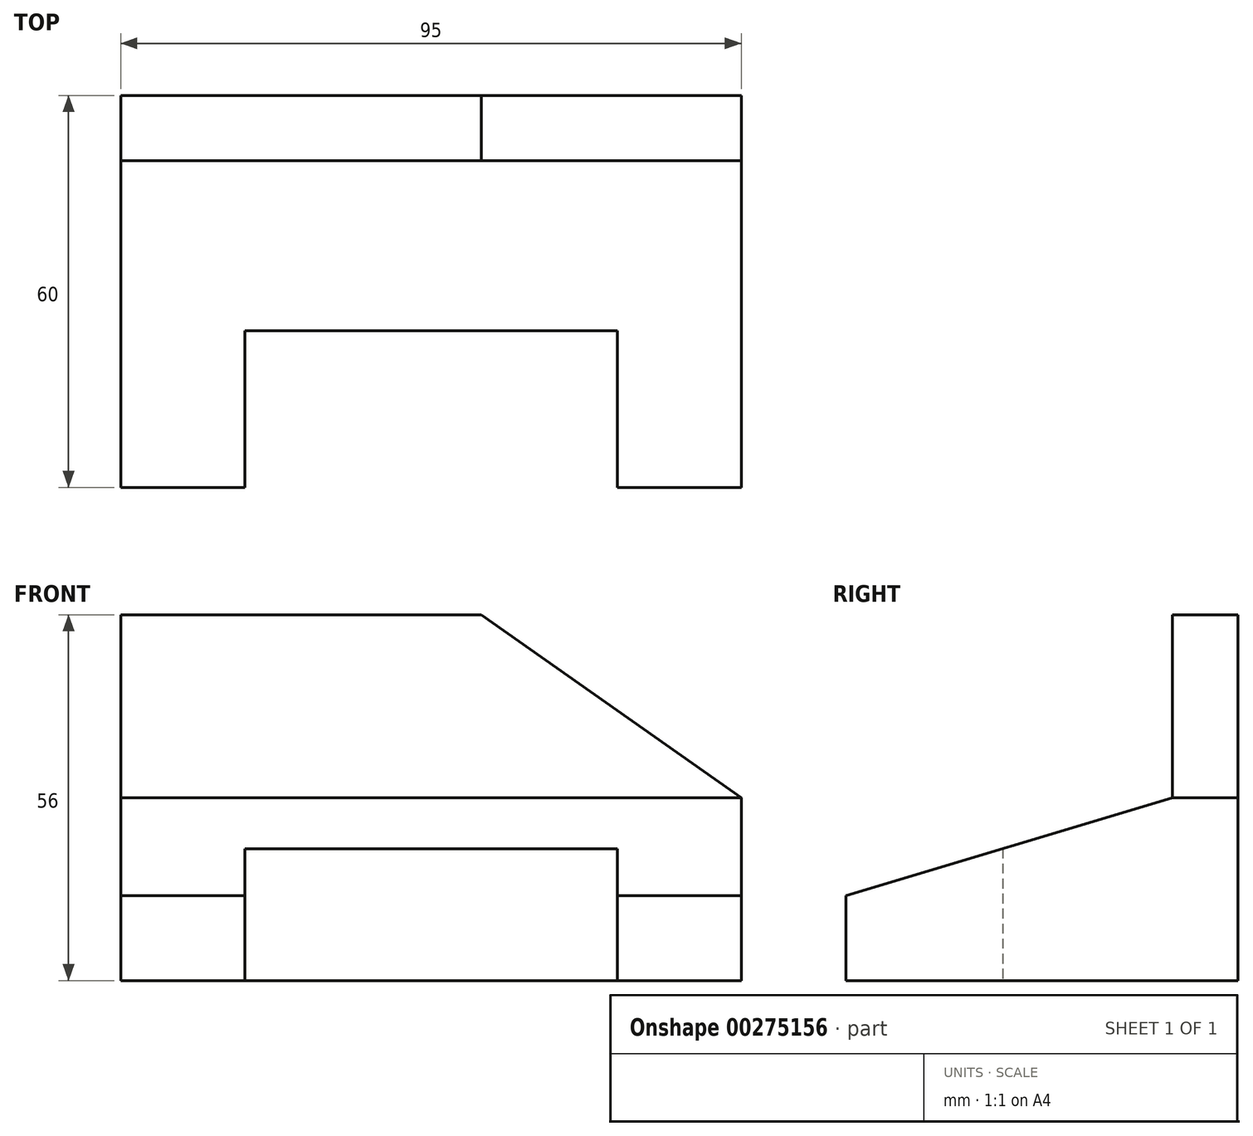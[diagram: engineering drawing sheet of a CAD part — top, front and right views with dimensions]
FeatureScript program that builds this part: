
annotation { "Feature Type Name" : "Feature", "Feature Type Description" : "" }
export const myFeature = defineFeature(function(context is Context, id is Id, definition is map)
    precondition{}
    {
        {
            var Q0;
            Q0=qCreatedBy(makeId("Right.planeOp"),FACE);
            var sketch = newSketch(context, id + "F0", { "sketchPlane" : qUnion([Q0])});
            skLineSegment(sketch, "E0", {"start": v(0, 0) * mm, "end": v(-60, 0) * mm});
            skLineSegment(sketch, "E1", {"start": v(-60, 0) * mm, "end": v(-60, 13) * mm});
            skLineSegment(sketch, "E2", {"start": v(-60, 13) * mm, "end": v(-10, 28) * mm});
            skLineSegment(sketch, "E3", {"start": v(-10, 28) * mm, "end": v(-10, 56) * mm});
            skLineSegment(sketch, "E4", {"start": v(-10, 56) * mm, "end": v(0, 56) * mm});
            skLineSegment(sketch, "E5", {"start": v(0, 56) * mm, "end": v(0, 0) * mm});
            skSolve(sketch);
        }
        {
            var Q0;
            Q0 = qSketchRegion(id + "F0", true);
            extrude(context, id + "F1", {"entities" : qUnion([Q0]), "depth" : 95 * mm});
        }
        {
            var Q0;
            Q0=makeQuery(id+"F1.opExtrude","SWEPT_FACE",FACE,{"disambiguationData":[OSD([sQuery(id+"F0.wireOp",EDGE,"E3")])]});
            var sketch = newSketch(context, id + "F2", { "sketchPlane" : qUnion([Q0])});
            skLineSegment(sketch, "E6", {"start": v(95, 28) * mm, "end": v(55.18, 56) * mm});
            skSolve(sketch);
        }
        {
            var Q0;
            {var subQ0=sQuery(id+"F2.wireOp",EDGE,"E6");Q0=makeQuery(id+"F2.imprint","IMPRINT",FACE,{"disambiguationData":[TD([[makeQuery(id+"F2.imprint","IMPRINT",EDGE,{"derivedFrom":subQ0}),-1.0]])]});}
            extrude(context, id + "F3", {"entities" : qUnion([Q0]), "operationType" : NewBodyOperationType.REMOVE, "endBound" : BoundingType.THROUGH_ALL, "oppositeDirection" : true, "depth" : 25 * mm});
        }
        {
            var Q0;
            Q0=makeQuery(id+"F1.opExtrude","SWEPT_FACE",FACE,{"disambiguationData":[OSD([sQuery(id+"F0.wireOp",EDGE,"E0")])]});
            var sketch = newSketch(context, id + "F4", { "sketchPlane" : qUnion([Q0])});
            skLineSegment(sketch, "E7.bottom", {"start": v(76, 36) * mm, "end": v(19, 36) * mm});
            skLineSegment(sketch, "E7.top", {"start": v(76, 60) * mm, "end": v(19, 60) * mm});
            skLineSegment(sketch, "E7.left", {"start": v(76, 36) * mm, "end": v(76, 60) * mm});
            skLineSegment(sketch, "E7.right", {"start": v(19, 36) * mm, "end": v(19, 60) * mm});
            skSolve(sketch);
        }
        {
            var Q0;
            Q0=makeQuery(id+"F4.imprint","IMPRINT",FACE,{"disambiguationData":[TD([[makeQuery(id+"F4.imprint","IMPRINT",EDGE,{"derivedFrom":sQuery(id+"F4.wireOp",EDGE,"E7.bottom")}),-1.0]])]});
            extrude(context, id + "F5", {"entities" : qUnion([Q0]), "operationType" : NewBodyOperationType.REMOVE, "oppositeDirection" : true, "depth" : 25 * mm});
        }
    });
